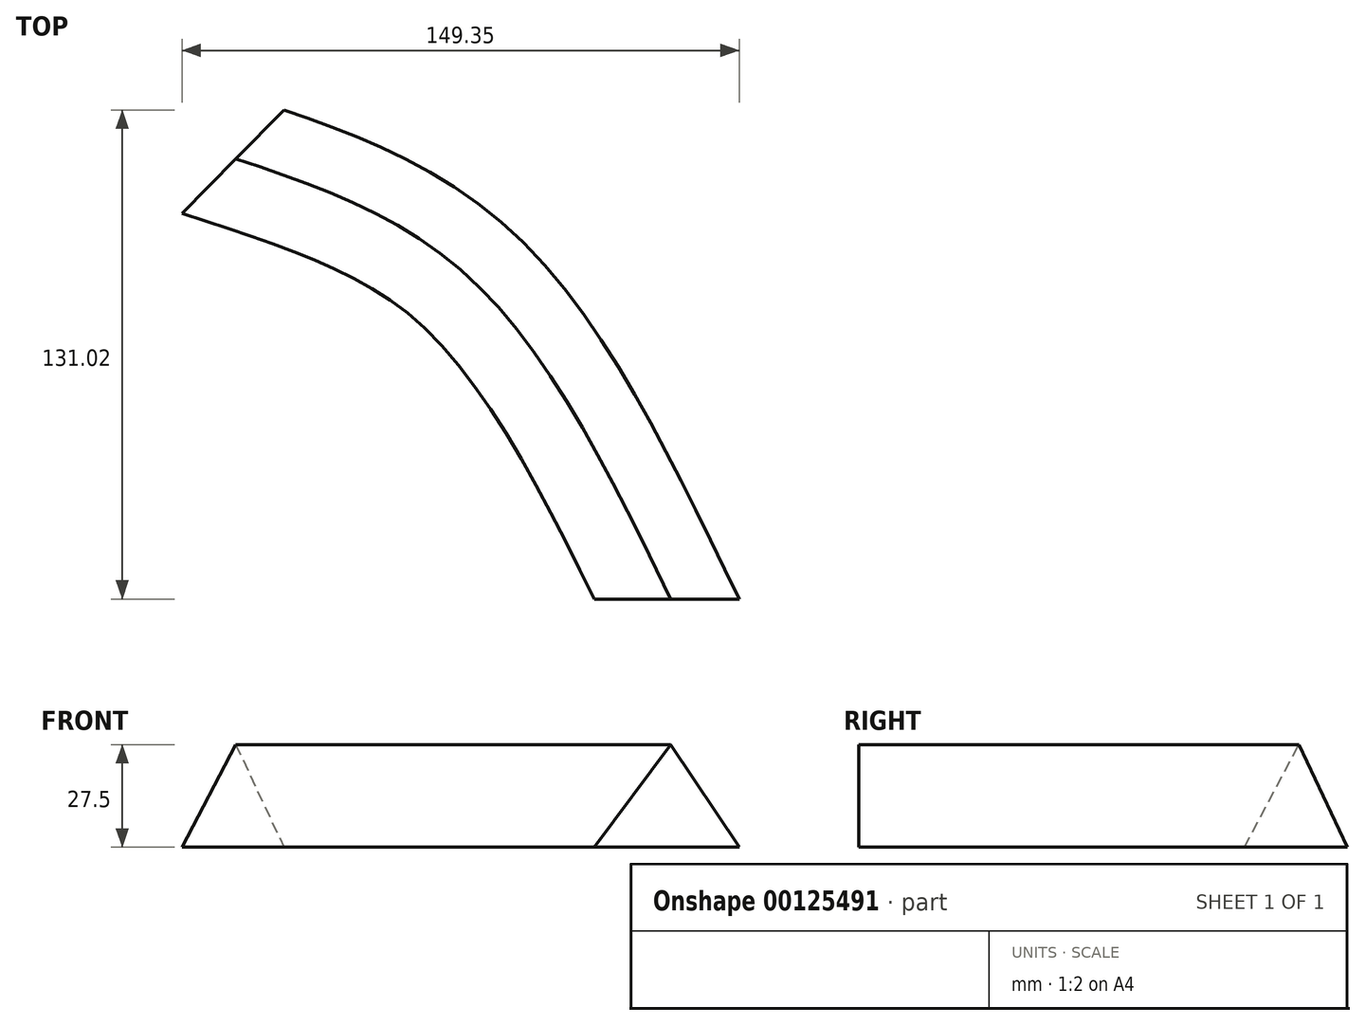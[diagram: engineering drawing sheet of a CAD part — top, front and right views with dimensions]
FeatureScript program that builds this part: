
annotation { "Feature Type Name" : "Feature", "Feature Type Description" : "" }
export const myFeature = defineFeature(function(context is Context, id is Id, definition is map)
    precondition{}
    {
        {
            var Q0;
            Q0=qCreatedBy(makeId("Front.planeOp"),FACE);
            var sketch = newSketch(context, id + "F0", { "sketchPlane" : qUnion([Q0])});
            skLineSegment(sketch, "E0", {"start": v(0, 0) * mm, "end": v(20.53, 27.5) * mm});
            skLineSegment(sketch, "E1", {"start": v(20.53, 27.5) * mm, "end": v(38.87, 0) * mm});
            skLineSegment(sketch, "E2", {"start": v(38.87, 0) * mm, "end": v(0, 0) * mm});
            skSolve(sketch);
        }
        {
            var Q0;
            Q0=qCreatedBy(makeId("Top.planeOp"),FACE);
            var sketch = newSketch(context, id + "F1", { "sketchPlane" : qUnion([Q0])});
            skFitSpline(sketch, "E3", {"points": [v(19.49, 0) * mm, v(9.1, 85.08) * mm, v(35.08, 118.24) * mm], "startDerivative": vector(-41.38, 163.6) * mm, "endDerivative": vector(79.65, 67.22) * mm});
            skFitSpline(sketch, "E4", {"points": [v(19.49, 0) * mm, v(-34.61, 85.92) * mm, v(-96.78, 117.24) * mm], "startDerivative": vector(-88.4, 181.12) * mm, "endDerivative": vector(-145.95, 49.22) * mm});
            skSolve(sketch);
        }
        {
            var Q0;
            Q0=makeQuery(id+"F0.imprint","IMPRINT",FACE,{"disambiguationData":[TD([[makeQuery(id+"F0.imprint","IMPRINT",EDGE,{"derivedFrom":sQuery(id+"F0.wireOp",EDGE,"E0")}),-1.0]])]});
            var Q1;
            Q1=sQuery(id+"F1.wireOp",EDGE,"E4");
            sweep(context, id + "F2", {"profiles" : qUnion([Q0]), "path" : qUnion([Q1])});
        }
    });
